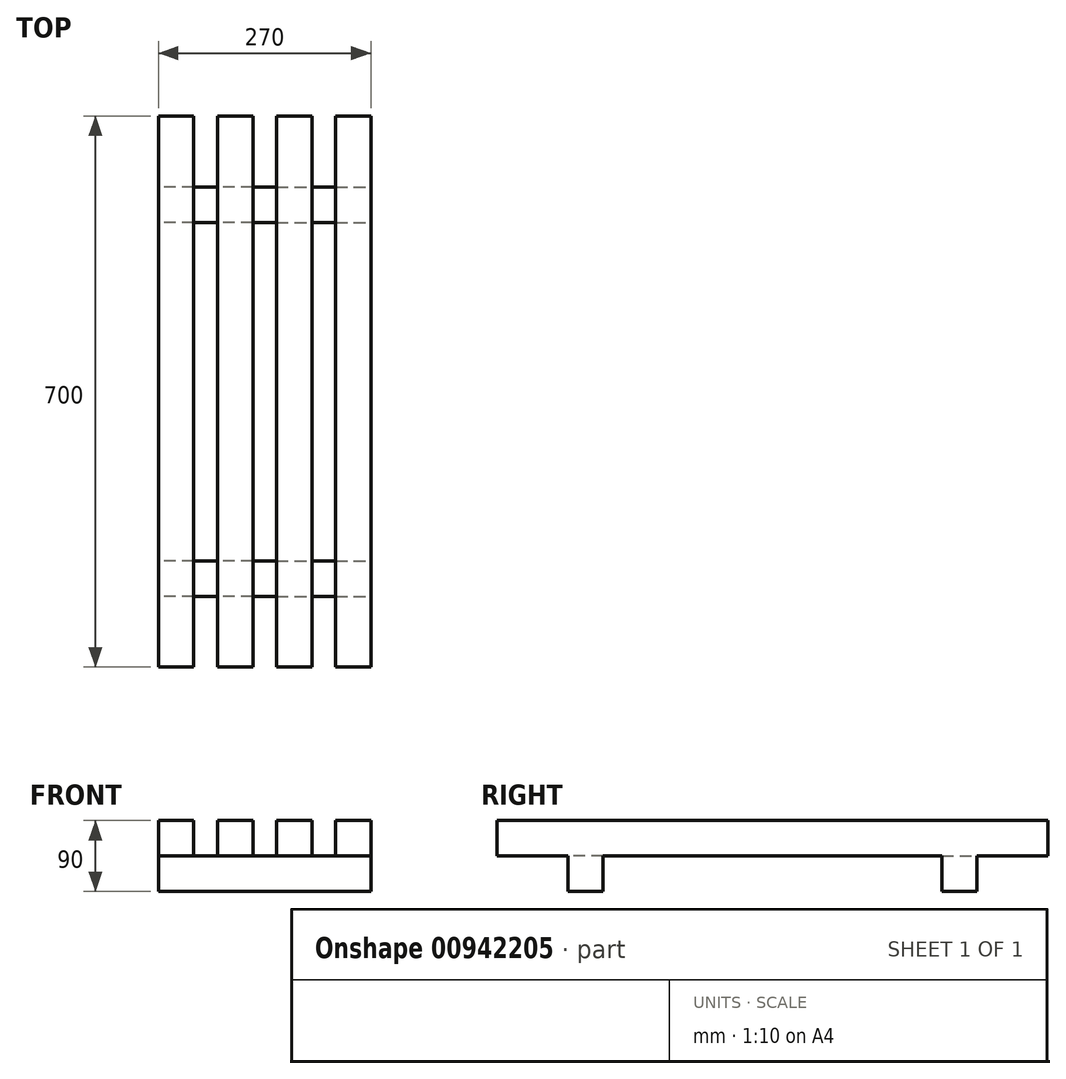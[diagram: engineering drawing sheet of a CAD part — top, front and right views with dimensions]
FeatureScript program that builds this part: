
annotation { "Feature Type Name" : "Feature", "Feature Type Description" : "" }
export const myFeature = defineFeature(function(context is Context, id is Id, definition is map)
    precondition{}
    {
        {
            var Q0;
            Q0=qCreatedBy(makeId("Top.planeOp"),FACE);
            var sketch = newSketch(context, id + "F0", { "sketchPlane" : qUnion([Q0])});
            skLineSegment(sketch, "E0", {"start": v(0, 0) * mm, "end": v(15, 0) * mm, "construction": true});
            skLineSegment(sketch, "E1.bottom", {"start": v(15, 0) * mm, "end": v(60, 0) * mm});
            skLineSegment(sketch, "E1.top", {"start": v(15, 350) * mm, "end": v(60, 350) * mm});
            skLineSegment(sketch, "E1.left", {"start": v(15, 0) * mm, "end": v(15, 350) * mm});
            skLineSegment(sketch, "E1.right", {"start": v(60, 0) * mm, "end": v(60, 350) * mm});
            skLineSegment(sketch, "E2", {"start": v(60, 0) * mm, "end": v(90, 0) * mm, "construction": true});
            skLineSegment(sketch, "E3", {"start": v(0, 0) * mm, "end": v(0, 350) * mm, "construction": true});
            skLineSegment(sketch, "E4.bottom", {"start": v(90, 0) * mm, "end": v(135, 0) * mm});
            skLineSegment(sketch, "E4.top", {"start": v(90, 350) * mm, "end": v(135, 350) * mm});
            skLineSegment(sketch, "E4.left", {"start": v(90, 0) * mm, "end": v(90, 350) * mm});
            skLineSegment(sketch, "E4.right", {"start": v(135, 0) * mm, "end": v(135, 350) * mm});
            skSolve(sketch);
        }
        {
            var Q0;
            Q0=qCreatedBy(makeId("Top.planeOp"),FACE);
            var sketch = newSketch(context, id + "F1", { "sketchPlane" : qUnion([Q0])});
            skLineSegment(sketch, "E5.bottom", {"start": v(0, 215) * mm, "end": v(135, 215) * mm});
            skLineSegment(sketch, "E5.top", {"start": v(0, 260) * mm, "end": v(135, 260) * mm});
            skLineSegment(sketch, "E5.left", {"start": v(0, 215) * mm, "end": v(0, 260) * mm});
            skLineSegment(sketch, "E5.right", {"start": v(135, 215) * mm, "end": v(135, 260) * mm});
            skSolve(sketch);
        }
        {
            var Q0;
            Q0=makeQuery(id+"F0.imprint","IMPRINT",FACE,{"disambiguationData":[TD([[makeQuery(id+"F0.imprint","IMPRINT",EDGE,{"derivedFrom":sQuery(id+"F0.wireOp",EDGE,"E4.bottom")}),1.0]])]});
            var Q1;
            Q1=makeQuery(id+"F0.imprint","IMPRINT",FACE,{"disambiguationData":[TD([[makeQuery(id+"F0.imprint","IMPRINT",EDGE,{"derivedFrom":sQuery(id+"F0.wireOp",EDGE,"E1.bottom")}),1.0]])]});
            extrude(context, id + "F2", {"entities" : qUnion([Q0, Q1]), "depth" : 45 * mm, "offsetDistance" : 25 * mm});
        }
        {
            var Q0;
            Q0=makeQuery(id+"F1.imprint","IMPRINT",FACE,{"disambiguationData":[TD([[makeQuery(id+"F1.imprint","IMPRINT",EDGE,{"derivedFrom":sQuery(id+"F1.wireOp",EDGE,"E5.bottom")}),1.0]])]});
            extrude(context, id + "F3", {"entities" : qUnion([Q0]), "oppositeDirection" : true, "depth" : 45 * mm, "offsetDistance" : 25 * mm});
        }
        {
            var Q0;
            Q0=makeQuery(id+"F3.opExtrude","SWEPT_BODY",BODY,{"disambiguationData":[OSD([sQuery(id+"F1.wireOp",EDGE,"E5.bottom"),sQuery(id+"F1.wireOp",EDGE,"E5.top"),sQuery(id+"F1.wireOp",EDGE,"E5.left"),sQuery(id+"F1.wireOp",EDGE,"E5.right")])]});
            var Q1;
            Q1=makeQuery(id+"F2.opExtrude","SWEPT_BODY",BODY,{"disambiguationData":[OSD([sQuery(id+"F0.wireOp",EDGE,"E1.bottom"),sQuery(id+"F0.wireOp",EDGE,"E1.top"),sQuery(id+"F0.wireOp",EDGE,"E1.left"),sQuery(id+"F0.wireOp",EDGE,"E1.right")])]});
            var Q2;
            Q2=makeQuery(id+"F2.opExtrude","SWEPT_BODY",BODY,{"disambiguationData":[OSD([sQuery(id+"F0.wireOp",EDGE,"E4.bottom"),sQuery(id+"F0.wireOp",EDGE,"E4.top"),sQuery(id+"F0.wireOp",EDGE,"E4.left"),sQuery(id+"F0.wireOp",EDGE,"E4.right")])]});
            var Q3;
            Q3=qCreatedBy(makeId("Front.planeOp"),FACE);
            mirror(context, id + "F4", {"operationType" : NewBodyOperationType.ADD, "entities" : qUnion([Q0, Q1, Q2]), "mirrorPlane" : qUnion([Q3])});
        }
        {
            var Q0;
            Q0=makeQuery(id+"F2.opExtrude","SWEPT_BODY",BODY,{"disambiguationData":[OSD([sQuery(id+"F0.wireOp",EDGE,"E1.bottom"),sQuery(id+"F0.wireOp",EDGE,"E1.top"),sQuery(id+"F0.wireOp",EDGE,"E1.left"),sQuery(id+"F0.wireOp",EDGE,"E1.right")])]});
            var Q1;
            Q1=makeQuery(id+"F3.opExtrude","SWEPT_BODY",BODY,{"disambiguationData":[OSD([sQuery(id+"F1.wireOp",EDGE,"E5.bottom"),sQuery(id+"F1.wireOp",EDGE,"E5.top"),sQuery(id+"F1.wireOp",EDGE,"E5.left"),sQuery(id+"F1.wireOp",EDGE,"E5.right")])]});
            var Q2;
            Q2=qCreatedBy(makeId("Right.planeOp"),FACE);
            mirror(context, id + "F5", {"operationType" : NewBodyOperationType.ADD, "entities" : qUnion([Q0, Q1]), "mirrorPlane" : qUnion([Q2])});
        }
    });
